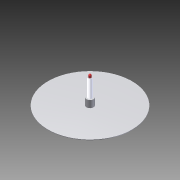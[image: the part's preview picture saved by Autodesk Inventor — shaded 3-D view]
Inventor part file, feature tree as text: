
AUTODESK INVENTOR PART (.ipt)
format: ipt  version: 2012 (Build 160160000, 160)  size: 96,256 bytes
history: native  units: mm
features: extrude x4, sketch x4, fillet x1
ambient origin geometry x8: Origin, YZ Plane, XZ Plane, XY Plane, X Axis, Y Axis, Z Axis, Center Point
bodies: Solid1 (feature_tree)
feature tree (9):
  extrude  "Extrusion1"  Depth=4.0mm TaperAngle=0.0deg
  sketch  "Sketch2"  dims[d3=50.0mm d4=30.0mm]
  extrude  "Extrusion2"  Depth=30.0mm
  extrude  "Extrusion3"  Depth=174.0mm TaperAngle=0.0deg
  extrude  "Extrusion4"  Depth=20.0mm TaperAngle=0.0deg
  fillet  "Fillet1"  Radius=9.0mm
  sketch  "Sketch4"  dims[d9=18.0mm d10=20.0mm d11=0.0mm d12=9.0mm]
  sketch  "Sketch1"  dims[d0=600.0mm d1=4.0mm d2=0.0mm]
  sketch  "Sketch3"  dims[d5=50.0mm d6=0.0mm d7=174.0mm d8=0.0mm]
